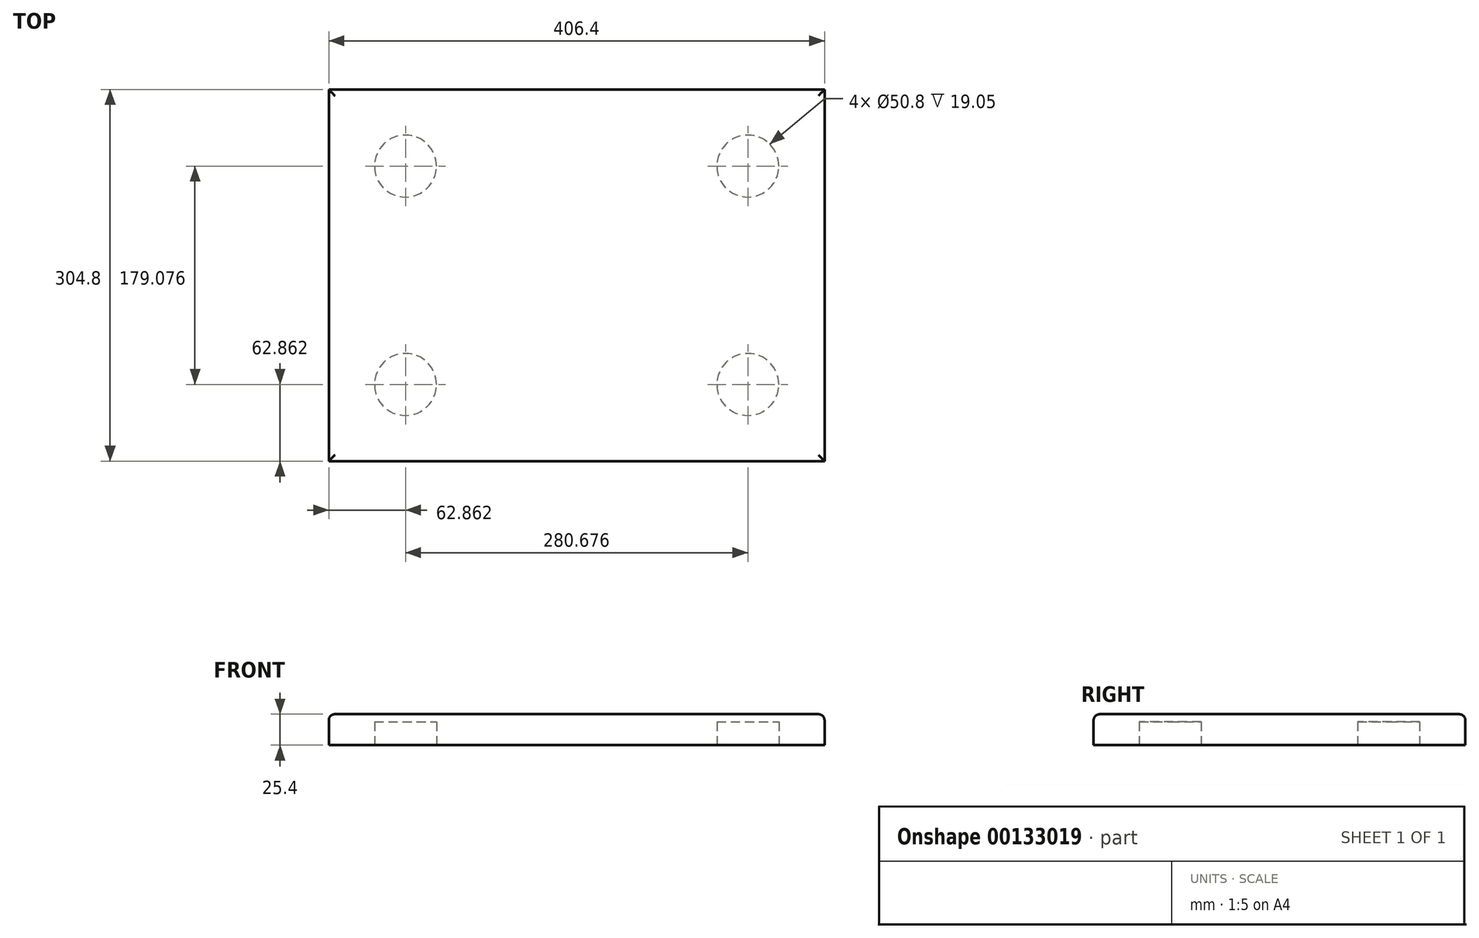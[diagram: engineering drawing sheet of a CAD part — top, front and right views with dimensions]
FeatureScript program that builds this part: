
annotation { "Feature Type Name" : "Feature", "Feature Type Description" : "" }
export const myFeature = defineFeature(function(context is Context, id is Id, definition is map)
    precondition{}
    {
        {
            var Q0;
            Q0=qCreatedBy(makeId("Top.planeOp"),FACE);
            var sketch = newSketch(context, id + "F0", { "sketchPlane" : qUnion([Q0])});
            skLineSegment(sketch, "E0.bottom", {"start": v(-203.2, 152.4) * mm, "end": v(203.2, 152.4) * mm});
            skLineSegment(sketch, "E0.top", {"start": v(-203.2, -152.4) * mm, "end": v(203.2, -152.4) * mm});
            skLineSegment(sketch, "E0.left", {"start": v(-203.2, 152.4) * mm, "end": v(-203.2, -152.4) * mm});
            skLineSegment(sketch, "E0.right", {"start": v(203.2, 152.4) * mm, "end": v(203.2, -152.4) * mm});
            skPoint(sketch, "E0.middle", {"position": v(0, 0) * mm});
            skSolve(sketch);
        }
        {
            var Q0;
            Q0 = qSketchRegion(id + "F0", true);
            extrude(context, id + "F1", {"entities" : qUnion([Q0]), "oppositeDirection" : true, "depth" : 25.4 * mm});
        }
        {
            var Q0;
            Q0=makeQuery(id+"F1.opExtrude","CAP_EDGE",EDGE,{"disambiguationData":[OSD([sQuery(id+"F0.wireOp",EDGE,"E0.top")])],"isStart":true});
            var Q1;
            Q1=makeQuery(id+"F1.opExtrude","CAP_EDGE",EDGE,{"disambiguationData":[OSD([sQuery(id+"F0.wireOp",EDGE,"E0.right")])],"isStart":true});
            var Q2;
            Q2=makeQuery(id+"F1.opExtrude","CAP_EDGE",EDGE,{"disambiguationData":[OSD([sQuery(id+"F0.wireOp",EDGE,"E0.bottom")])],"isStart":true});
            var Q3;
            Q3=makeQuery(id+"F1.opExtrude","CAP_EDGE",EDGE,{"disambiguationData":[OSD([sQuery(id+"F0.wireOp",EDGE,"E0.left")])],"isStart":true});
            fillet(context, id + "F2", {"entities" : qUnion([Q0, Q1, Q2, Q3]), "radius" : 5.08 * mm, "tangentPropagation" : true, "allowEdgeOverflow" : false});
        }
        {
            var Q0;
            Q0=makeQuery(id+"F1.opExtrude","CAP_FACE",FACE,{"disambiguationData":[OSD([sQuery(id+"F0.wireOp",EDGE,"E0.bottom"),sQuery(id+"F0.wireOp",EDGE,"E0.top"),sQuery(id+"F0.wireOp",EDGE,"E0.left"),sQuery(id+"F0.wireOp",EDGE,"E0.right")])],"isStart":false});
            var sketch = newSketch(context, id + "F3", { "sketchPlane" : qUnion([Q0])});
            skLineSegment(sketch, "E1", {"start": v(-203.2, 152.4) * mm, "end": v(-140.34, 89.54) * mm, "construction": true});
            skCircle(sketch, "E2", {"center": v(-140.34, 89.54) * mm, "radius": 25.4 * mm});
            skCircle(sketch, "E3.MirrorC", {"center": v(140.34, 89.54) * mm, "radius": 25.4 * mm});
            skCircle(sketch, "E4.MirrorC", {"center": v(-140.34, -89.54) * mm, "radius": 25.4 * mm});
            skCircle(sketch, "E5.MirrorC", {"center": v(140.34, -89.54) * mm, "radius": 25.4 * mm});
            skSolve(sketch);
        }
        {
            var Q0;
            Q0 = qSketchRegion(id + "F3", true);
            extrude(context, id + "F4", {"entities" : qUnion([Q0]), "operationType" : NewBodyOperationType.REMOVE, "oppositeDirection" : true, "depth" : 19.05 * mm});
        }
    });
